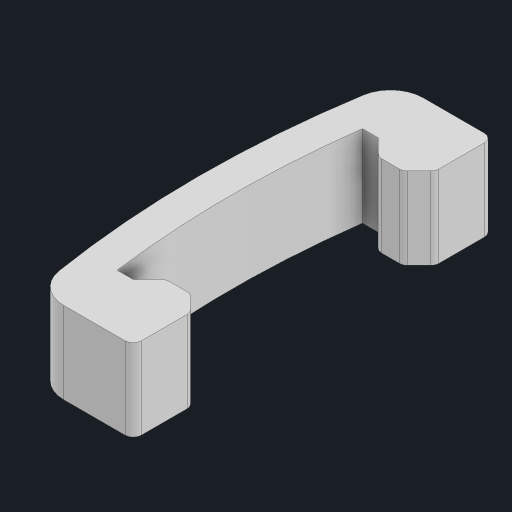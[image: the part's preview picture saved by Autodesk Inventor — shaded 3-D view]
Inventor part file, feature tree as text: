
AUTODESK INVENTOR PART (.ipt)
format: ipt  version: 2023.1 (Build 271208000, 208)  size: 152,576 bytes
history: native  units: mm
features: fillet x2, extrude x1, mirror x1, sketch x1
ambient origin geometry x8: Origin, YZ Plane, XZ Plane, XY Plane, X Axis, Y Axis, Z Axis, Center Point
bodies: Solid1 (feature_tree)
feature tree (5):
  extrude  "Extrusion1"  Depth=2.0mm
  mirror  "Mirror1"
  fillet  "Fillet1"  Radius=1.0mm
  fillet  "Fillet2"  [1 undecoded]
  sketch  "Sketch1"  dims[d0=4.3mm d1=20.0mm d2=20.0mm d3=5.0mm d4=6.4mm d5=11.5mm d6=2.0mm d8=1.0mm d9=45.0deg d10=45.0deg d11=3.0mm d12=1.5mm d13=0.5mm d14=0.5mm d15=5.0mm d16=0.0mm d17=2.0mm d18=0.5mm]
note: 1 required parameter value undecoded (feature->parameter linkage not recoverable at this tier; creation-order binding heuristic only, values carry confidence <= 0.55)
